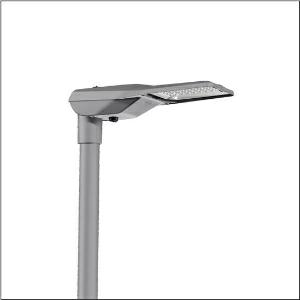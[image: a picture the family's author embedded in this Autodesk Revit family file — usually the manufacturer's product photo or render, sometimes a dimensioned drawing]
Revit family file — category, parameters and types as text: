
# Revit family: streetlight_sl_21_iq_mini___st0_5a_5xe2b31y08gb_b50d
name_source: partatom
category: Lighting Fixtures
units: mm (PartAtom-declared; Revit-internal decimal feet)

## family parameters
Cut with Voids When Loaded = No
Host = Face
Light Source = No
Part Type = Normal
Room Calculation Point = No
Round Connector Dimension = Use Diameter
Shared = No

## types (1)
- --- (1 x LED, 5990 lm, 39.8 W, 3000K)
    Apparent Load = 40 VA
    CIE Flux Codes = 41 75 97 100 100
    Color Rendering = 70
    Color Temperature = 3000K
    Default Elevation = 1800 mm
    Description = Streetlight SL 21 iQ mini, mast luminaire, primary light control with lens, of PMMA, primary optical cover: cover, of toughened safety glass, transparent, light distribution: ST0.5a, light emission: direct distribution, primary light characteristic: asymmetric, installation type: post-top, side-entry, LED, High Power LED, rated luminous flux: 5.990lm, luminous efficacy: 151lm/W, light colour: 730, colour temperature: 3000K, control: presetting dimming logarithmic, Street-Remote, Auto-Match, Temp-Guard, Lumen-Switch, Night-Set, Smart-Wire, Light-Fading, Desk-Remote (wireless, voltage-free reading and setting of iQ features in the workshop via application-optimized NFC function/RFID function), optimised constant luminous flux control (CLO 2.0), mains connection: 220..240V, AC, 50/60Hz, start of lifetime: 40W, end of service life: 41W, reduction: 18W, luminaire housing, of diecast aluminium, powder-coated, Siteco® metallic grey (DB 702S), corrosivity category C5 mid according to DIN EN ISO 12944, please order mast flange separately, inclination adjustable: 0°, 5°, 10°, 15°, sealing non-destructively replaceable, multi-level sealing system, length: 628mm, width: 235mm, height: 110mm, mast flange for spigot size: 42mm (side-entry): 5XC10008XM4, 60/48mm (side-entry/post-top): 5XC10108XM2, 76/60mm (side-entry/post-top): 5XC10108XM1, Smart Interface below and above, protection rating (complete): IP66, insulation class (complete): insulation class II (safety insulation), certification: CE, ENEC, ENEC+, VDE, impact resistance: IK09, permissible operating ambient temperature for outdoor applications: -40..+50°C, standard-compliant lighting for roads and squares, packaging unit: 1 piece

Light Distribution: ST0.5a
    Height = 110 mm
    Lamp = 1 x LED
    Lamp Light Flux = 5990 lm
    Lamp Power = 39.8 W
    Lamp count = 1
    Length = 625 mm
    Luminous efficacy = 151 lm/W
    Manufacturer = Siteco
    ModVariant = No
    Model = 5XE2B31Y08GB
    Number of Poles = 1
    OnlyDefault = Yes
    Power Factor = 1
    Product Name = Streetlight SL 21 iQ mini | ST0.5a
    Product group = mast luminaire | pylon top
    ProductGroupID = 6100
    Protection Class = Protection class II
    Protection Degree = IP 66
    RLX_Detail_Level = 1
    RLX_Emergency_Light_Flux = 0 lm
    RLX_Emergency_Type = 0
    RLX_Emergency_Type_DB = No
    RlxData = <blob elided: 103689 chars, md5=d98f3ef2>
    Socket = socket
    Standby Power = 0 W
    System Light Flux = 5990 lm
    System Power = 40 W
    Type Comments = factory setting: luminous flux: 100 % | dim-lin: 254 | 800 mA
    Type Image = l_1003514.jpg
    URL = http://relux.com
    VarID = @adj_046181
    Voltage = 0 V
    Weight = 0.00 kg
    Width = 234 mm

## geometry (parser evidence)
native form markers: Blend x4, Sweep x9
no freeform markers — native parametric forms only
